# Revit family: Projection_Screen-Draper_Inc-Acumen_V
name_source: partatom
category: Specialty Equipment
units: mm (PartAtom-declared; Revit-internal decimal feet)

## family parameters
Always vertical = Yes
Classification Number = 23.85.10.14.31
Cut with Voids When Loaded = No
Enable Cutting in Views = No
Maintain Annotation Orientation = No
Part Type = Normal
Room Calculation Point = No
Round Connector Dimension = Use Diameter
Shared = No
Work Plane-Based = No

## types (1)
- NOT A TYPE - LOAD TYPE CATALOG
    Apparent Load = 132 VA
    Case Color = Paint - Draper - Case - White
    Case Length = 8' - 9 1/4"
    Default Elevation = 0"
    Depth = 5 15/16"
    Description = Surface-Mounted, tab-tensioned Projection Screen
    Frequency = 60 Hz
    Image Height = 4' - 2"
    Image Width = 6' - 8"
    Manufacturer = Draper Inc.
    Model = Acumen V
    Number of Poles = 1
    Options = Recharge V - Battery Operated projection screen
    Product Documentation Link = https://www.draperinc.com
    Product Name = Acumen™ V Electric Projection Screen
    Product Page URL = https://www.draperinc.com
    Projection Screen Material = Fabric - Draper - XT1000VB - Matt White
    Screen Width = 7' - 3"
    Type Comments = Black drop will afffect case length, Contact Draper for more information.
    URL = http://www.DraperInc.com
    Version = 2019-v1.0a
    Voltage = 110 V
    Width = 7 1/8"

## geometry (parser evidence)
native form markers: Sweep x5
no freeform markers — native parametric forms only
